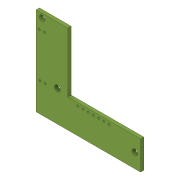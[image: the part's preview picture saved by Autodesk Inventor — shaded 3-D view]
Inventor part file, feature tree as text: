
AUTODESK INVENTOR PART (.ipt)
format: ipt  version: 2017 (Build 210142000, 142)  size: 169,984 bytes
history: native  units: in
note: dims shown in document units (in); Inventor stores cm internally (conversion verified against a paired STEP export)
features: reference x10, extrude x7, sketch x7, other x4
ambient origin geometry x8: Origin, YZ Plane, XZ Plane, XY Plane, X Axis, Y Axis, Z Axis, Center Point
bodies: Solid1 (feature_tree)
feature tree (28):
  extrude  "Extrusion1"  Depth=1.394in
  extrude  "Extrusion2"  Depth=0.55in
  extrude  "Extrusion3"  Depth=0.063in TaperAngle=0.0deg
  extrude  "Extrusion4"  Depth=0.2098in
  extrude  "Extrusion5"  Depth=0.035in
  extrude  "Extrusion6"  Depth=0.1in
  extrude  "Extrusion7"  Depth=0.5563in
  sketch  "Sketch1"  dims[d0=1.143in d1=1.394in]
  reference  "Reference1"
  sketch  "Sketch2"  dims[d2=0.606in d3=0.55in]
  reference  "Reference2"
  reference  "Reference3"
  reference  "Reference4"
  reference  "Reference5"
  reference  "Reference6"
  reference  "Reference7"
  reference  "Reference8"
  sketch  "Sketch4"  dims[d4=0.063in d5=0.0in d6=0.063in d7=0.0in]
  sketch  "Sketch5"  dims[d8=0.1732in d9=0.2098in]
  reference  "Reference9"
  sketch  "Sketch6"  dims[d10=0.035in d11=0.035in]
  sketch  "Sketch7"  dims[d12=0.0752in d13=0.1in]
  reference  "Reference10"
  sketch  "Sketch8"  dims[d14=0.0in d15=0.5563in d16=1.0in d17=0.0in d18=1.0in d19=0.0in d20=0.11in d21=1.0in d22=0.0in d23=0.11in d24=0.136in d25=1.0in d26=0.0in d27=0.11in d28=1.0in d29=0.0in]
  parser-record x1  (decoder bookkeeping rows leaked as tree rows — omitted from the tree; the rows remain in map.json)
  other  "Assembly1.iam"
  other  "Main PCB:1"
  other  "Faceplate:1"
note: 1 file-system path scrubbed to <path> (originals preserved in map.json)
